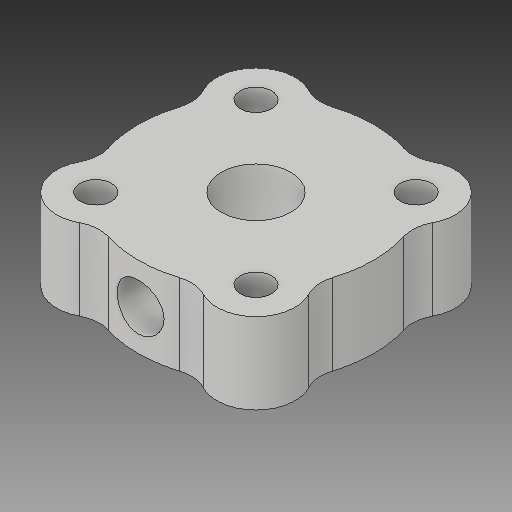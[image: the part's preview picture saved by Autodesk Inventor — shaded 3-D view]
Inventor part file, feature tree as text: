
AUTODESK INVENTOR PART (.ipt)
format: ipt  version: 2017 (Build 210142000, 142)  size: 160,256 bytes
history: native  units: in
note: dims shown in document units (in); Inventor stores cm internally (conversion verified against a paired STEP export)
features: fillet x1
ambient origin geometry x8: Origin, YZ Plane, XZ Plane, XY Plane, X Axis, Y Axis, Z Axis, Center Point
bodies: Solid1 (feature_tree)
feature tree (1):
  fillet  "Fillet1"  [1 undecoded]
note: 1 required parameter value undecoded (feature->parameter linkage not recoverable at this tier; creation-order binding heuristic only, values carry confidence <= 0.55)
